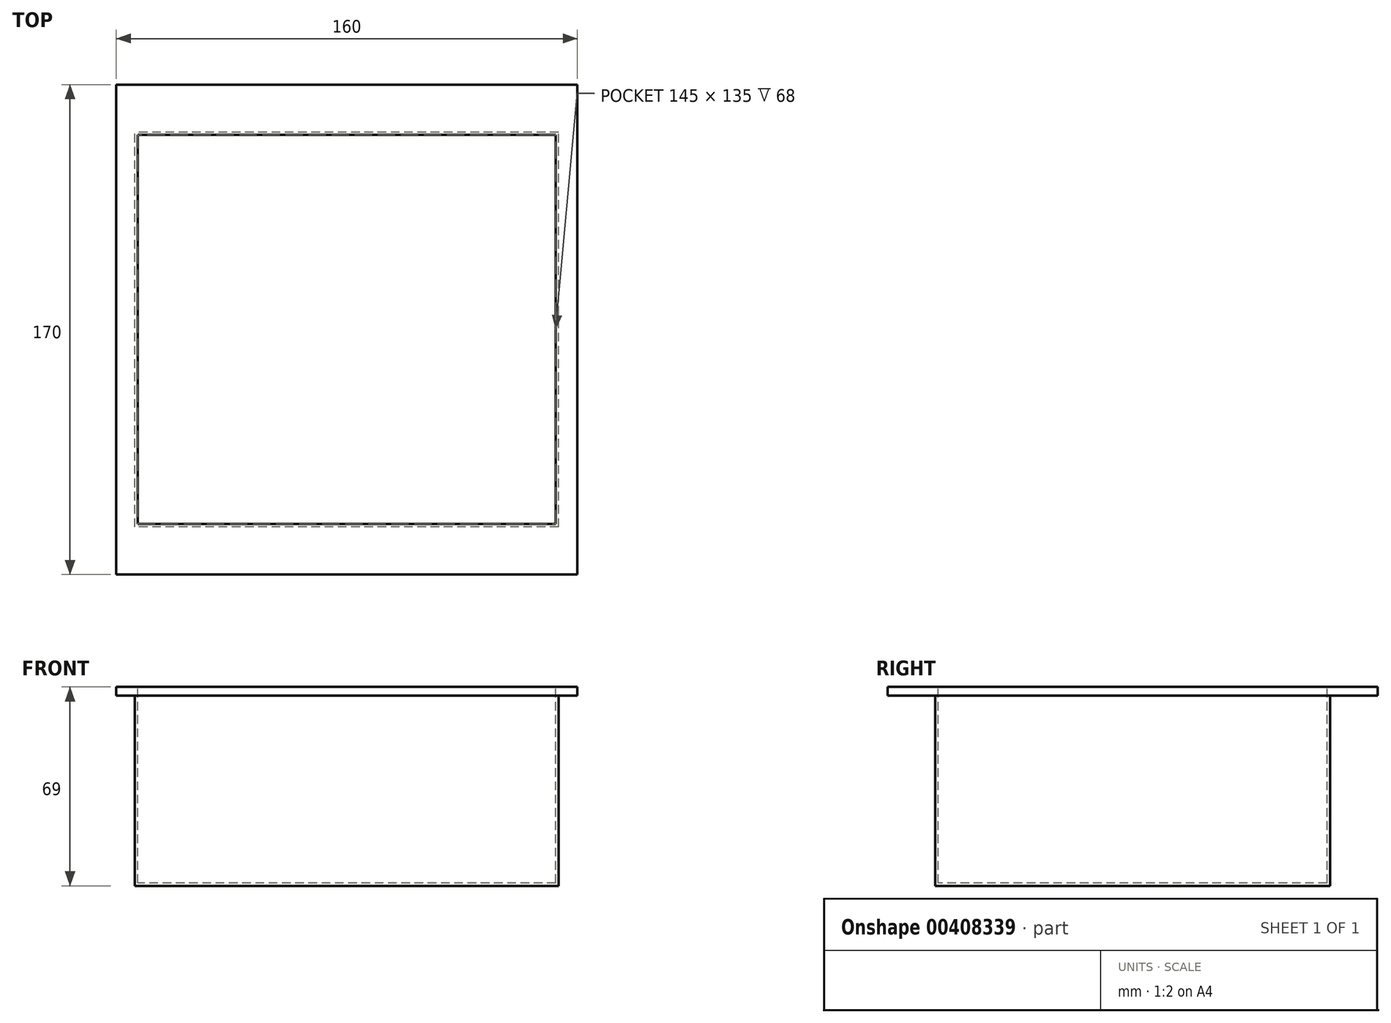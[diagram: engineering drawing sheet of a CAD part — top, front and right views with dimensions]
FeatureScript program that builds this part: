
annotation { "Feature Type Name" : "Feature", "Feature Type Description" : "" }
export const myFeature = defineFeature(function(context is Context, id is Id, definition is map)
    precondition{}
    {
        {
            var Q0;
            Q0=qCreatedBy(makeId("Top.planeOp"),FACE);
            var sketch = newSketch(context, id + "F0", { "sketchPlane" : qUnion([Q0])});
            skLineSegment(sketch, "E0.bottom", {"start": v(80, 85) * mm, "end": v(-80, 85) * mm});
            skLineSegment(sketch, "E0.top", {"start": v(80, -85) * mm, "end": v(-80, -85) * mm});
            skLineSegment(sketch, "E0.left", {"start": v(80, 85) * mm, "end": v(80, -85) * mm});
            skLineSegment(sketch, "E0.right", {"start": v(-80, 85) * mm, "end": v(-80, -85) * mm});
            skPoint(sketch, "E0.middle", {"position": v(0, 0) * mm});
            skLineSegment(sketch, "E1.bottom", {"start": v(72.5, 67.5) * mm, "end": v(-72.5, 67.5) * mm});
            skLineSegment(sketch, "E1.top", {"start": v(72.5, -67.5) * mm, "end": v(-72.5, -67.5) * mm});
            skLineSegment(sketch, "E1.left", {"start": v(72.5, 67.5) * mm, "end": v(72.5, -67.5) * mm});
            skLineSegment(sketch, "E1.right", {"start": v(-72.5, 67.5) * mm, "end": v(-72.5, -67.5) * mm});
            skSolve(sketch);
        }
        {
            var Q0;
            Q0=makeQuery(id+"F0.imprint","IMPRINT",FACE,{"disambiguationData":[TD([[makeQuery(id+"F0.imprint","IMPRINT",EDGE,{"derivedFrom":sQuery(id+"F0.wireOp",EDGE,"E0.bottom")}),1.0]])]});
            extrude(context, id + "F1", {"entities" : qUnion([Q0]), "oppositeDirection" : true, "depth" : 3 * mm});
        }
        {
            var Q0;
            Q0=makeQuery(id+"F1.opExtrude","CAP_FACE",FACE,{"disambiguationData":[OSD([sQuery(id+"F0.wireOp",EDGE,"E0.bottom"),sQuery(id+"F0.wireOp",EDGE,"E0.top"),sQuery(id+"F0.wireOp",EDGE,"E0.left"),sQuery(id+"F0.wireOp",EDGE,"E0.right"),sQuery(id+"F0.wireOp",EDGE,"E1.bottom"),sQuery(id+"F0.wireOp",EDGE,"E1.top"),sQuery(id+"F0.wireOp",EDGE,"E1.left"),sQuery(id+"F0.wireOp",EDGE,"E1.right")])],"isStart":false});
            var sketch = newSketch(context, id + "F2", { "sketchPlane" : qUnion([Q0])});
            skLineSegment(sketch, "E2.bottom", {"start": v(72.5, 67.5) * mm, "end": v(-72.5, 67.5) * mm});
            skLineSegment(sketch, "E2.top", {"start": v(72.5, -67.5) * mm, "end": v(-72.5, -67.5) * mm});
            skLineSegment(sketch, "E2.left", {"start": v(72.5, 67.5) * mm, "end": v(72.5, -67.5) * mm});
            skLineSegment(sketch, "E2.right", {"start": v(-72.5, 67.5) * mm, "end": v(-72.5, -67.5) * mm});
            skPoint(sketch, "E2.middle", {"position": v(0, 0) * mm});
            skLineSegment(sketch, "E3.0", {"start": v(73.5, 68.5) * mm, "end": v(73.5, -68.5) * mm});
            skLineSegment(sketch, "E3.1", {"start": v(73.5, 68.5) * mm, "end": v(-73.5, 68.5) * mm});
            skLineSegment(sketch, "E3.2", {"start": v(-73.5, 68.5) * mm, "end": v(-73.5, -68.5) * mm});
            skLineSegment(sketch, "E3.3", {"start": v(73.5, -68.5) * mm, "end": v(-73.5, -68.5) * mm});
            skSolve(sketch);
        }
        {
            var Q0;
            Q0=makeQuery(id+"F2.imprint","IMPRINT",FACE,{"disambiguationData":[TD([[makeQuery(id+"F2.imprint","IMPRINT",EDGE,{"derivedFrom":sQuery(id+"F2.wireOp",EDGE,"E2.bottom")}),-1.0]])]});
            extrude(context, id + "F3", {"entities" : qUnion([Q0]), "operationType" : NewBodyOperationType.ADD, "depth" : 65 * mm});
        }
        {
            var Q0;
            Q0=makeQuery(id+"F3.opExtrude","CAP_FACE",FACE,{"disambiguationData":[OSD([sQuery(id+"F2.wireOp",EDGE,"E2.bottom"),sQuery(id+"F2.wireOp",EDGE,"E2.top"),sQuery(id+"F2.wireOp",EDGE,"E2.left"),sQuery(id+"F2.wireOp",EDGE,"E2.right"),sQuery(id+"F2.wireOp",EDGE,"E3.0"),sQuery(id+"F2.wireOp",EDGE,"E3.1"),sQuery(id+"F2.wireOp",EDGE,"E3.2"),sQuery(id+"F2.wireOp",EDGE,"E3.3")])],"isStart":false});
            var sketch = newSketch(context, id + "F4", { "sketchPlane" : qUnion([Q0])});
            skLineSegment(sketch, "E4.bottom", {"start": v(73.5, 68.5) * mm, "end": v(-73.5, 68.5) * mm});
            skLineSegment(sketch, "E4.top", {"start": v(73.5, -68.5) * mm, "end": v(-73.5, -68.5) * mm});
            skLineSegment(sketch, "E4.left", {"start": v(73.5, 68.5) * mm, "end": v(73.5, -68.5) * mm});
            skLineSegment(sketch, "E4.right", {"start": v(-73.5, 68.5) * mm, "end": v(-73.5, -68.5) * mm});
            skPoint(sketch, "E4.middle", {"position": v(0, 0) * mm});
            skSolve(sketch);
        }
        {
            var Q0;
            Q0 = qSketchRegion(id + "F4", true);
            extrude(context, id + "F5", {"entities" : qUnion([Q0]), "operationType" : NewBodyOperationType.ADD, "depth" : 1 * mm});
        }
    });
